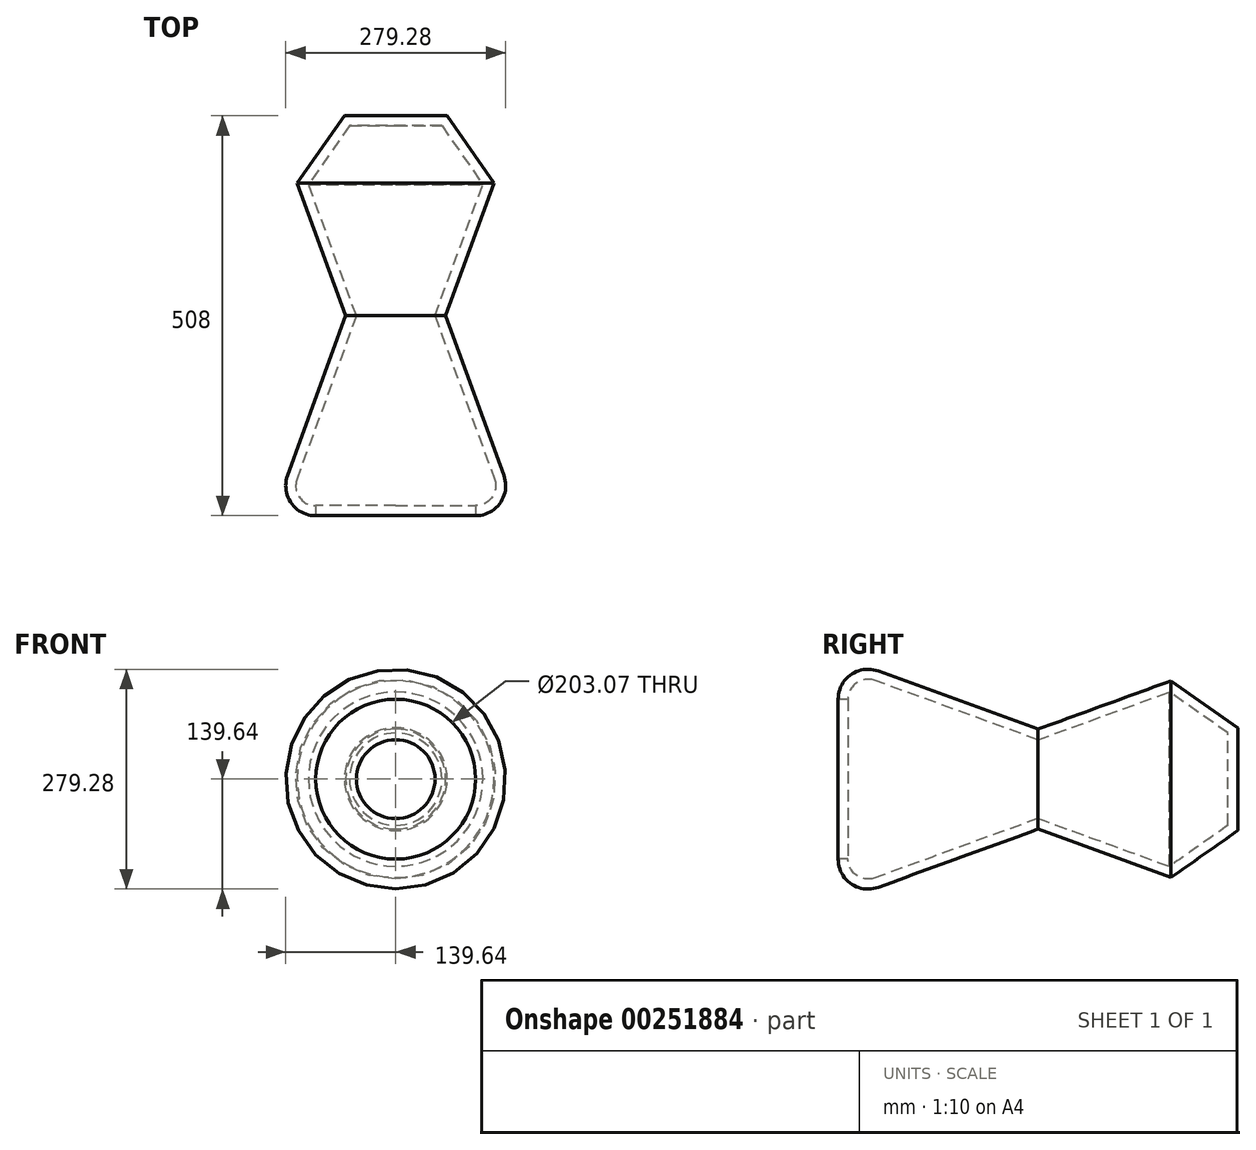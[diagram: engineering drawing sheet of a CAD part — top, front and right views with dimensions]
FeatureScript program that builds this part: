
annotation { "Feature Type Name" : "Feature", "Feature Type Description" : "" }
export const myFeature = defineFeature(function(context is Context, id is Id, definition is map)
    precondition{}
    {
        {
            var Q0;
            Q0=qCreatedBy(makeId("Front.planeOp"),FACE);
            var sketch = newSketch(context, id + "F0", { "sketchPlane" : qUnion([Q0])});
            skCircle(sketch, "E0", {"center": v(0, 0) * mm, "radius": 63.5 * mm});
            skSolve(sketch);
        }
        {
            var Q0;
            Q0=makeQuery(id+"F0.imprint","IMPRINT",FACE,{"disambiguationData":[TD([[makeQuery(id+"F0.imprint","IMPRINT",EDGE,{"derivedFrom":sQuery(id+"F0.wireOp",EDGE,"E0")}),1.0]])]});
            extrude(context, id + "F1", {"entities" : qUnion([Q0]), "depth" : 254 * mm, "hasDraft" : true, "draftAngle" : 20 * degree});
        }
        {
            var Q0;
            Q0=makeQuery(id+"F1.opExtrude","CAP_FACE",FACE,{"disambiguationData":[OSD([sQuery(id+"F0.wireOp",EDGE,"E0")])],"isStart":true});
            extrude(context, id + "F2", {"entities" : qUnion([Q0]), "operationType" : NewBodyOperationType.ADD, "depth" : 254 * mm, "hasDraft" : true, "draftAngle" : 20 * degree});
        }
        {
            var Q0;
            Q0=makeQuery(id+"F1.opExtrude","CAP_EDGE",EDGE,{"disambiguationData":[OSD([sQuery(id+"F0.wireOp",EDGE,"E0")])],"isStart":false});
            fillet(context, id + "F3", {"entities" : qUnion([Q0]), "radius" : 38.1 * mm, "tangentPropagation" : true, "allowEdgeOverflow" : false});
        }
        {
            var Q0;
            Q0=makeQuery(id+"F2.opExtrude","CAP_EDGE",EDGE,{"disambiguationData":[OSD([sQuery(id+"F0.wireOp",EDGE,"E0")])],"isStart":false});
            chamfer(context, id + "F4", {"entities" : qUnion([Q0]), "width" : 63.5 * mm, "tangentPropagation" : true});
        }
        {
            var Q0;
            Q0=makeQuery(id+"F1.opExtrude","CAP_FACE",FACE,{"disambiguationData":[OSD([sQuery(id+"F0.wireOp",EDGE,"E0")])],"isStart":false});
            shell(context, id + "F5", {"entities" : qUnion([Q0]), "thickness" : 12.7 * mm});
        }
    });
